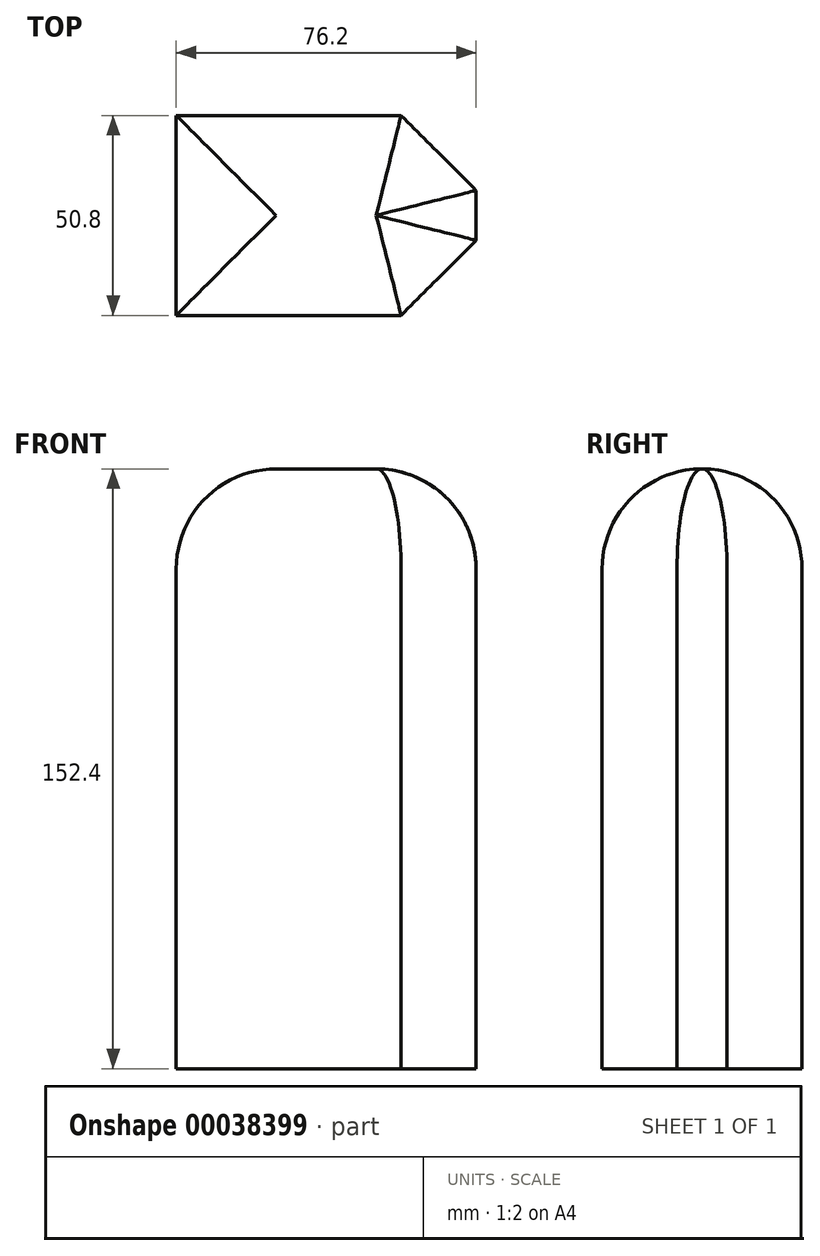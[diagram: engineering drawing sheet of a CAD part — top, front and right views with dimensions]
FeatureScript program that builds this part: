
annotation { "Feature Type Name" : "Feature", "Feature Type Description" : "" }
export const myFeature = defineFeature(function(context is Context, id is Id, definition is map)
    precondition{}
    {
        {
            var Q0;
            Q0=qCreatedBy(makeId("Top.planeOp"),FACE);
            var sketch = newSketch(context, id + "F0", { "sketchPlane" : qUnion([Q0])});
            skLineSegment(sketch, "E0.bottom", {"start": v(0, 0) * mm, "end": v(76.2, 0) * mm});
            skLineSegment(sketch, "E0.top", {"start": v(0, 50.8) * mm, "end": v(76.2, 50.8) * mm});
            skLineSegment(sketch, "E0.left", {"start": v(0, 0) * mm, "end": v(0, 50.8) * mm});
            skLineSegment(sketch, "E0.right", {"start": v(76.2, 0) * mm, "end": v(76.2, 50.8) * mm});
            skSolve(sketch);
        }
        {
            var Q0;
            Q0=makeQuery(id+"F0.imprint","IMPRINT",FACE,{"disambiguationData":[TD([[makeQuery(id+"F0.imprint","IMPRINT",EDGE,{"derivedFrom":sQuery(id+"F0.wireOp",EDGE,"E0.bottom")}),1.0]])]});
            extrude(context, id + "F1", {"entities" : qUnion([Q0]), "depth" : 152.4 * mm});
        }
        {
            var Q0;
            Q0=makeQuery(id+"F1.opExtrude","CAP_EDGE",EDGE,{"disambiguationData":[OSD([sQuery(id+"F0.wireOp",EDGE,"E0.right")])],"isStart":false});
            var Q1;
            Q1=makeQuery(id+"F1.opExtrude","CAP_EDGE",EDGE,{"disambiguationData":[OSD([sQuery(id+"F0.wireOp",EDGE,"E0.bottom")])],"isStart":false});
            var Q2;
            Q2=makeQuery(id+"F1.opExtrude","CAP_EDGE",EDGE,{"disambiguationData":[OSD([sQuery(id+"F0.wireOp",EDGE,"E0.left")])],"isStart":false});
            var Q3;
            Q3=makeQuery(id+"F1.opExtrude","CAP_EDGE",EDGE,{"disambiguationData":[OSD([sQuery(id+"F0.wireOp",EDGE,"E0.top")])],"isStart":false});
            fillet(context, id + "F2", {"entities" : qUnion([Q0, Q1, Q2, Q3]), "radius" : 25.4 * mm, "tangentPropagation" : true, "allowEdgeOverflow" : false});
        }
        {
            var Q0;
            Q0=makeQuery(id+"F1.opExtrude","SWEPT_EDGE",EDGE,{"disambiguationData":[OSD([sQuery(id+"F0.wireOp",EDGE,"E0.bottom"),sQuery(id+"F0.wireOp",EDGE,"E0.right")])]});
            var Q1;
            Q1=makeQuery(id+"F1.opExtrude","SWEPT_EDGE",EDGE,{"disambiguationData":[OSD([sQuery(id+"F0.wireOp",EDGE,"E0.top"),sQuery(id+"F0.wireOp",EDGE,"E0.right")])]});
            chamfer(context, id + "F3", {"entities" : qUnion([Q0, Q1]), "width" : 19.05 * mm, "tangentPropagation" : true});
        }
    });
